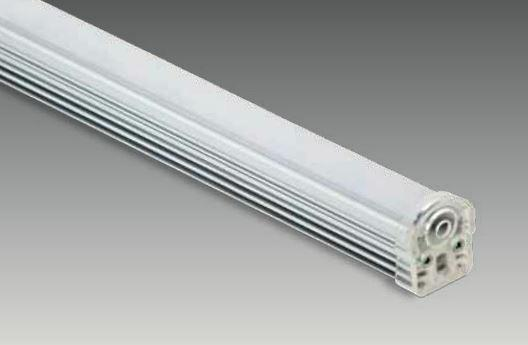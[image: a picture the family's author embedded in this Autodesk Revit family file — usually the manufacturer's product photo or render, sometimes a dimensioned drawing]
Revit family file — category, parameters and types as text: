
# Revit family: SD 0505 CVK
name_source: partatom
category: Lighting Fixtures
revit_build: Autodesk Revit 2017 (Build: 20160225_1515(x64)
units: mm (PartAtom-declared; Revit-internal decimal feet)

## family parameters
Cut with Voids When Loaded = No
Host = Face
Light Source = Yes
Part Type = Normal
Room Calculation Point = No
Round Connector Dimension = Use Diameter
Shared = No

## types (2) — shared parameters
Apparent Load = 12 VA
Color Filter = 16777215
Default Elevation = 1219 mm
Dimming Lamp Color Temperature Shift = <None>
Emit Shape Visible in Rendering = Yes
Emit from Rectangle Length = 15 mm  [stored 0.0492126 ft]
Emit from Rectangle Width = 500 mm  [stored 1.64042 ft]
Light Source Symbol Size = 610 mm
Manufacturer = ARLIGHT
Type Image = SD 0505 CVK.JPG
Wattage Comments = 12

## type names (no varying parameters)
- SDCVK.505.12.30
- SDCVK.505.12.40

note: [stored X ft] marks values corroborated as IEEE doubles in the binary element streams (Revit-internal decimal feet)

## geometry (parser evidence)
native form markers: Sweep x3
no freeform markers — native parametric forms only
